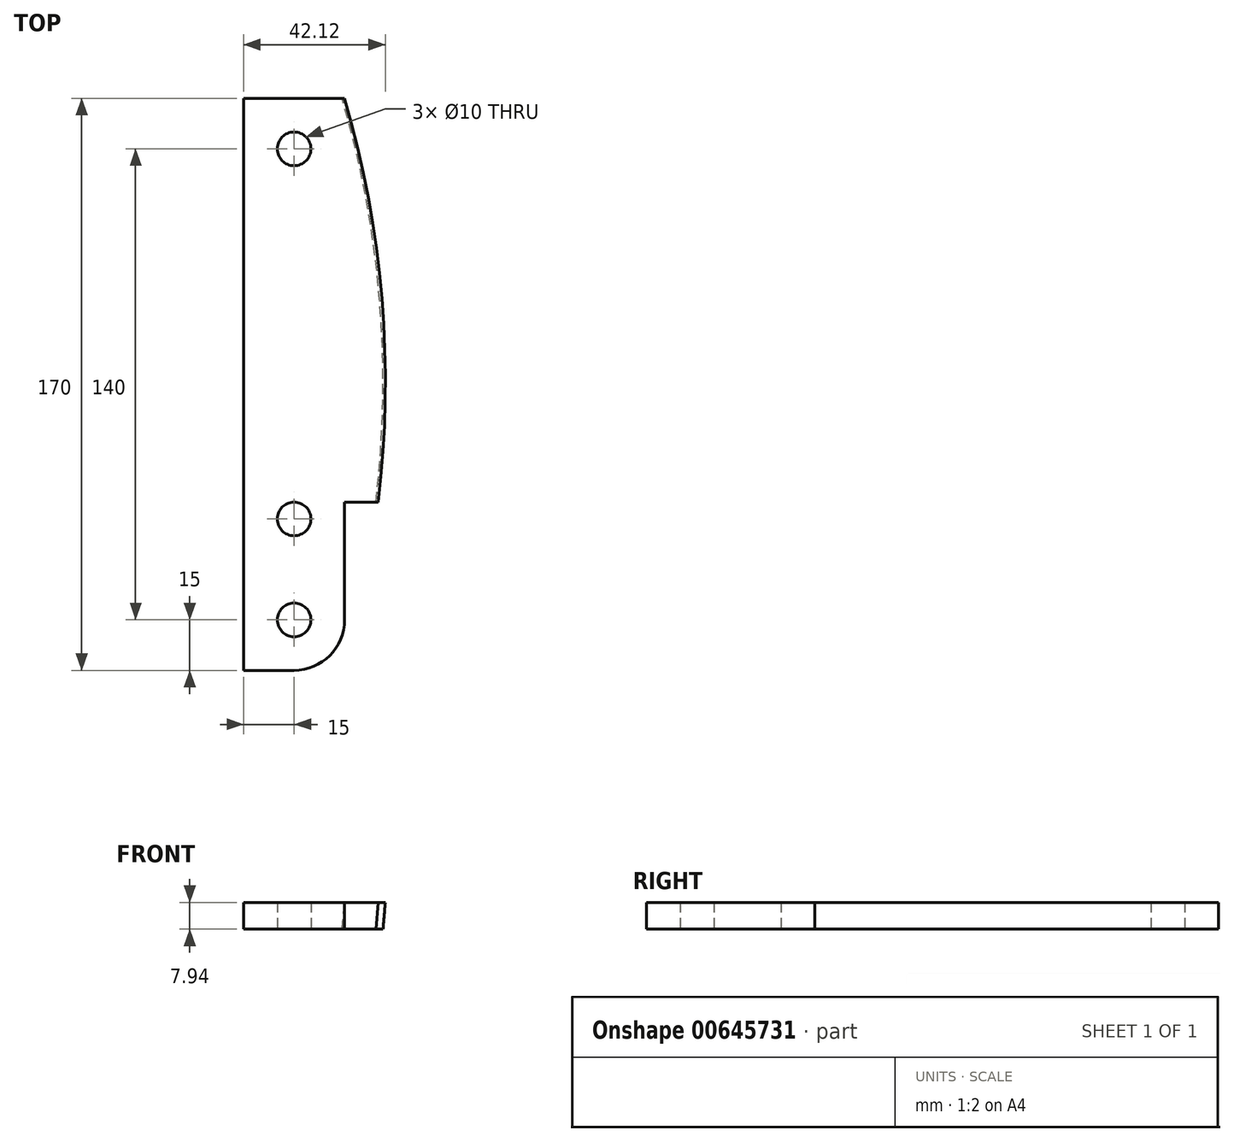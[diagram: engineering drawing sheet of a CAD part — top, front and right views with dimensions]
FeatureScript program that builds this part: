
annotation { "Feature Type Name" : "Feature", "Feature Type Description" : "" }
export const myFeature = defineFeature(function(context is Context, id is Id, definition is map)
    precondition{}
    {
        {
            var Q0;
            Q0=qCreatedBy(makeId("Top.planeOp"),FACE);
            var sketch = newSketch(context, id + "F0", { "sketchPlane" : qUnion([Q0])});
            skLineSegment(sketch, "E0", {"start": v(0, 85) * mm, "end": v(0, -85) * mm});
            skLineSegment(sketch, "E1", {"start": v(30, 85) * mm, "end": v(0, 85) * mm});
            skLineSegment(sketch, "E2", {"start": v(0, -85) * mm, "end": v(15, -85) * mm});
            skArc(sketch, "E3", {"start": v(40, -35) * mm, "mid": v(41.08, 25.5) * mm, "end": v(30, 85) * mm});
            skLineSegment(sketch, "E4", {"start": v(30, -70) * mm, "end": v(30, -35) * mm});
            skLineSegment(sketch, "E5", {"start": v(30, -35) * mm, "end": v(40, -35) * mm});
            skPoint(sketch, "E6.visualSharp", {"position": v(30, -85) * mm});
            skArc(sketch, "E6.filletArc", {"start": v(15, -85) * mm, "mid": v(25.6, -80.6) * mm, "end": v(30, -70) * mm});
            skCircle(sketch, "E7", {"center": v(15, -70) * mm, "radius": 5 * mm});
            skCircle(sketch, "E8", {"center": v(15, -40) * mm, "radius": 5 * mm});
            skCircle(sketch, "E9", {"center": v(15, 70) * mm, "radius": 5 * mm});
            skSolve(sketch);
        }
        {
            var Q0;
            Q0=makeQuery(id+"F0.imprint","IMPRINT",FACE,{"disambiguationData":[TD([[makeQuery(id+"F0.imprint","IMPRINT",EDGE,{"derivedFrom":sQuery(id+"F0.wireOp",EDGE,"E0")}),1.0]])]});
            extrude(context, id + "F1", {"entities" : qUnion([Q0]), "depth" : 7.94 * mm, "offsetDistance" : 25 * mm});
        }
        {
            var Q0;
            Q0=makeQuery(id+"F1.opExtrude","SWEPT_FACE",FACE,{"disambiguationData":[OSD([sQuery(id+"F0.wireOp",EDGE,"E5")])]});
            var sketch = newSketch(context, id + "F2", { "sketchPlane" : qUnion([Q0])});
            skLineSegment(sketch, "E10", {"start": v(40, 0) * mm, "end": v(40, 7.94) * mm});
            skLineSegment(sketch, "E11", {"start": v(40, 7.94) * mm, "end": v(39.3, 0) * mm});
            skLineSegment(sketch, "E12", {"start": v(39.3, 0) * mm, "end": v(40, 0) * mm});
            skSolve(sketch);
        }
        {
            var Q0;
            Q0=makeQuery(id+"F1.opExtrude","CAP_FACE",FACE,{"disambiguationData":[OSD([sQuery(id+"F0.wireOp",EDGE,"E0"),sQuery(id+"F0.wireOp",EDGE,"E1"),sQuery(id+"F0.wireOp",EDGE,"E2"),sQuery(id+"F0.wireOp",EDGE,"E3"),sQuery(id+"F0.wireOp",EDGE,"E4"),sQuery(id+"F0.wireOp",EDGE,"E5"),sQuery(id+"F0.wireOp",EDGE,"E6.filletArc"),sQuery(id+"F0.wireOp",EDGE,"E7"),sQuery(id+"F0.wireOp",EDGE,"E8"),sQuery(id+"F0.wireOp",EDGE,"E9")])],"isStart":false});
            var sketch = newSketch(context, id + "F3", { "sketchPlane" : qUnion([Q0])});
            skArc(sketch, "E13.0", {"start": v(40, -35) * mm, "mid": v(41.08, 25.5) * mm, "end": v(30, 85) * mm});
            skArc(sketch, "E14", {"start": v(30, 85) * mm, "mid": v(29.69, 86.05) * mm, "end": v(29.37, 87.1) * mm});
            skSolve(sketch);
        }
        {
            var Q0;
            Q0 = qSketchRegion(id + "F2", true);
            var Q1;
            Q1 = qConstructionFilter(qBodyType(qCreatedBy(id + "F3" ,EDGE), BodyType.WIRE), ConstructionObject.NO);
            sweep(context, id + "F4", {"operationType" : NewBodyOperationType.REMOVE, "profiles" : qUnion([Q0]), "path" : qUnion([Q1])});
        }
    });
